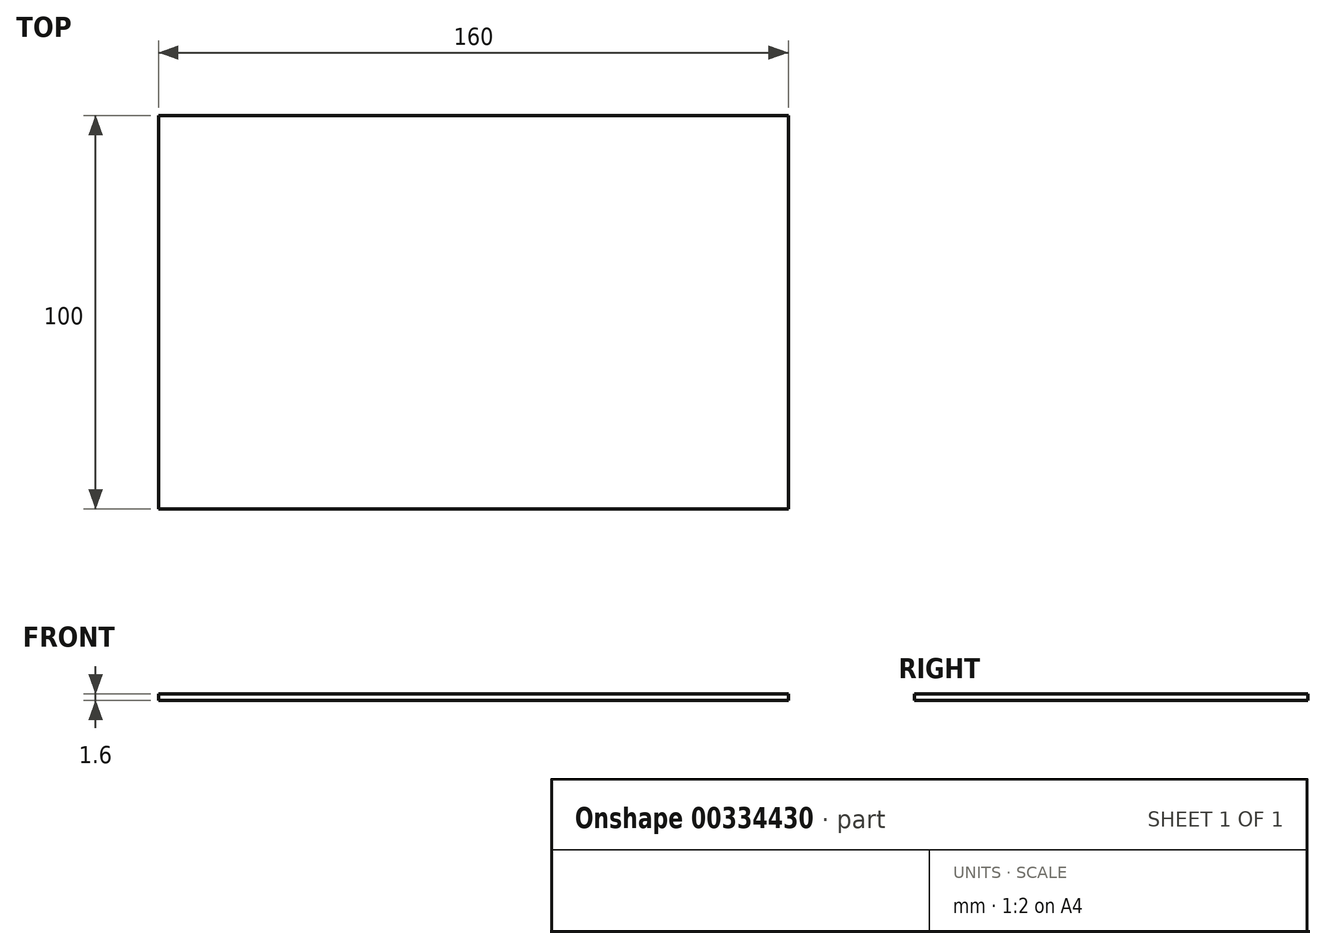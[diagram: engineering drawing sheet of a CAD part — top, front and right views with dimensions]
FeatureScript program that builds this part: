
annotation { "Feature Type Name" : "Feature", "Feature Type Description" : "" }
export const myFeature = defineFeature(function(context is Context, id is Id, definition is map)
    precondition{}
    {
        {
            var Q0;
            Q0=qCreatedBy(makeId("Top.planeOp"),FACE);
            var sketch = newSketch(context, id + "F0", { "sketchPlane" : qUnion([Q0])});
            skLineSegment(sketch, "E0.bottom", {"start": v(-80, 50) * mm, "end": v(80, 50) * mm});
            skLineSegment(sketch, "E0.top", {"start": v(-80, -50) * mm, "end": v(80, -50) * mm});
            skLineSegment(sketch, "E0.left", {"start": v(-80, 50) * mm, "end": v(-80, -50) * mm});
            skLineSegment(sketch, "E0.right", {"start": v(80, 50) * mm, "end": v(80, -50) * mm});
            skPoint(sketch, "E0.middle", {"position": v(0, 0) * mm});
            skSolve(sketch);
        }
        {
            var Q0;
            Q0=makeQuery(id+"F0.imprint","IMPRINT",FACE,{"disambiguationData":[TD([[makeQuery(id+"F0.imprint","IMPRINT",EDGE,{"derivedFrom":sQuery(id+"F0.wireOp",EDGE,"E0.bottom")}),-1.0]])]});
            extrude(context, id + "F1", {"entities" : qUnion([Q0]), "depth" : 1.6 * mm});
        }
    });
